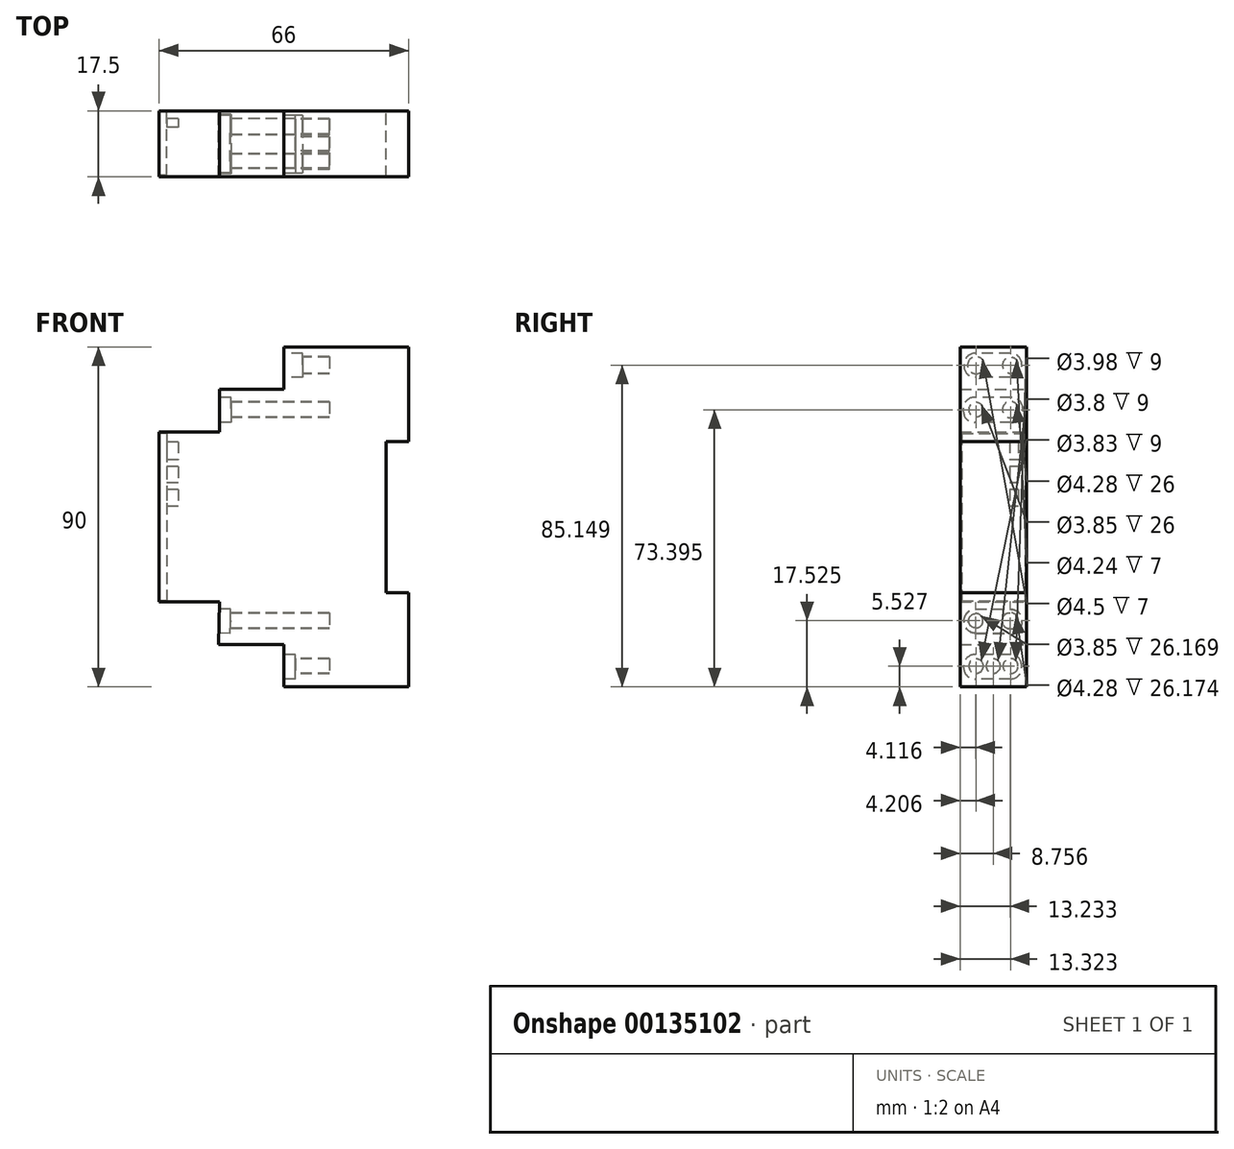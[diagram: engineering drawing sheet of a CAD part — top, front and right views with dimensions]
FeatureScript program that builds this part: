
annotation { "Feature Type Name" : "Feature", "Feature Type Description" : "" }
export const myFeature = defineFeature(function(context is Context, id is Id, definition is map)
    precondition{}
    {
        {
            var Q0;
            Q0=qCreatedBy(makeId("Front.planeOp"),FACE);
            var sketch = newSketch(context, id + "F0", { "sketchPlane" : qUnion([Q0])});
            skLineSegment(sketch, "E0.bottom", {"start": v(-62.04, 123.6) * mm, "end": v(-29.04, 123.6) * mm});
            skLineSegment(sketch, "E0.top", {"start": v(-62.04, 33.6) * mm, "end": v(-29.04, 33.6) * mm});
            skLineSegment(sketch, "E0.left", {"start": v(-95.04, 101.1) * mm, "end": v(-95.04, 56.1) * mm});
            skLineSegment(sketch, "E0.right", {"start": v(-29.04, 123.6) * mm, "end": v(-29.04, 98.6) * mm});
            skLineSegment(sketch, "E1", {"start": v(-62.04, 123.6) * mm, "end": v(-62.04, 112.34) * mm});
            skLineSegment(sketch, "E2", {"start": v(-62.04, 112.34) * mm, "end": v(-79.04, 112.34) * mm});
            skLineSegment(sketch, "E3", {"start": v(-79.04, 112.34) * mm, "end": v(-79.04, 101.1) * mm});
            skLineSegment(sketch, "E4", {"start": v(-79.04, 101.1) * mm, "end": v(-95.04, 101.1) * mm});
            skLineSegment(sketch, "E5", {"start": v(-95.04, 56.1) * mm, "end": v(-79.04, 56.1) * mm});
            skLineSegment(sketch, "E6", {"start": v(-79.04, 56.1) * mm, "end": v(-79.31, 44.84) * mm});
            skLineSegment(sketch, "E7", {"start": v(-79.31, 44.84) * mm, "end": v(-62.04, 44.84) * mm});
            skLineSegment(sketch, "E8", {"start": v(-62.04, 44.84) * mm, "end": v(-62.04, 33.6) * mm});
            skPoint(sketch, "E9.orphan", {"position": v(-95.04, 123.6) * mm});
            skPoint(sketch, "E10.orphan", {"position": v(-95.04, 33.6) * mm});
            skLineSegment(sketch, "E11", {"start": v(-29.04, 98.6) * mm, "end": v(-35.04, 98.6) * mm});
            skLineSegment(sketch, "E12", {"start": v(-35.04, 98.6) * mm, "end": v(-35.04, 58.6) * mm});
            skLineSegment(sketch, "E13", {"start": v(-35.04, 58.6) * mm, "end": v(-29.04, 58.6) * mm});
            skLineSegment(sketch, "E14.trimOffspring", {"start": v(-29.04, 58.6) * mm, "end": v(-29.04, 33.6) * mm});
            skSolve(sketch);
        }
        {
            var Q0;
            Q0=makeQuery(id+"F0.imprint","IMPRINT",FACE,{"disambiguationData":[TD([[makeQuery(id+"F0.imprint","IMPRINT",EDGE,{"derivedFrom":sQuery(id+"F0.wireOp",EDGE,"E0.bottom")}),-1.0]])]});
            extrude(context, id + "F1", {"entities" : qUnion([Q0]), "depth" : 17.5 * mm});
        }
        {
            var Q0;
            Q0=makeQuery(id+"F1.opExtrude","SWEPT_FACE",FACE,{"disambiguationData":[OSD([sQuery(id+"F0.wireOp",EDGE,"E0.left")])]});
            var sketch = newSketch(context, id + "F2", { "sketchPlane" : qUnion([Q0])});
            skCircle(sketch, "E15", {"center": v(4.18, 106.99) * mm, "radius": 2.14 * mm});
            skCircle(sketch, "E16", {"center": v(13.3, 106.99) * mm, "radius": 1.93 * mm});
            skCircle(sketch, "E17", {"center": v(13.3, 118.74) * mm, "radius": 2.25 * mm});
            skCircle(sketch, "E18", {"center": v(4.18, 118.74) * mm, "radius": 2.12 * mm});
            skCircle(sketch, "E19", {"center": v(4.18, 39.12) * mm, "radius": 1.99 * mm});
            skCircle(sketch, "E20", {"center": v(13.3, 39.12) * mm, "radius": 1.91 * mm});
            skCircle(sketch, "E21", {"center": v(8.74, 39.12) * mm, "radius": 1.9 * mm});
            skCircle(sketch, "E22", {"center": v(4.27, 51.11) * mm, "radius": 2.14 * mm});
            skCircle(sketch, "E23", {"center": v(13.38, 51.11) * mm, "radius": 1.93 * mm});
            skSolve(sketch);
        }
        {
            var Q0;
            Q0=makeQuery(id+"F1.opExtrude","SWEPT_FACE",FACE,{"disambiguationData":[OSD([sQuery(id+"F0.wireOp",EDGE,"E1")])]});
            var sketch = newSketch(context, id + "F3", { "sketchPlane" : qUnion([Q0])});
            skLineSegment(sketch, "E24.bottom", {"start": v(4.2, 121.92) * mm, "end": v(13.5, 121.92) * mm});
            skLineSegment(sketch, "E24.top", {"start": v(4.2, 115.51) * mm, "end": v(13.5, 115.51) * mm});
            skLineSegment(sketch, "E24.left", {"start": v(1.2, 118.92) * mm, "end": v(1.2, 118.51) * mm});
            skLineSegment(sketch, "E24.right", {"start": v(16.5, 118.92) * mm, "end": v(16.5, 118.51) * mm});
            skPoint(sketch, "E25.visualSharp", {"position": v(1.2, 121.92) * mm});
            skArc(sketch, "E25.filletArc", {"start": v(4.2, 121.92) * mm, "mid": v(2.09, 121.04) * mm, "end": v(1.2, 118.92) * mm});
            skPoint(sketch, "E26.visualSharp", {"position": v(1.2, 115.51) * mm});
            skArc(sketch, "E26.filletArc", {"start": v(1.2, 118.51) * mm, "mid": v(2.09, 116.39) * mm, "end": v(4.2, 115.51) * mm});
            skPoint(sketch, "E27.visualSharp", {"position": v(16.5, 115.51) * mm});
            skArc(sketch, "E27.filletArc", {"start": v(13.5, 115.51) * mm, "mid": v(15.61, 116.39) * mm, "end": v(16.5, 118.51) * mm});
            skPoint(sketch, "E28.visualSharp", {"position": v(16.5, 121.92) * mm});
            skArc(sketch, "E28.filletArc", {"start": v(16.5, 118.92) * mm, "mid": v(15.61, 121.04) * mm, "end": v(13.5, 121.92) * mm});
            skSolve(sketch);
        }
        {
            var Q0;
            Q0=makeQuery(id+"F3.imprint","IMPRINT",FACE,{"disambiguationData":[TD([[makeQuery(id+"F3.imprint","IMPRINT",EDGE,{"derivedFrom":sQuery(id+"F3.wireOp",EDGE,"E24.bottom")}),-1.0]])]});
            extrude(context, id + "F4", {"entities" : qUnion([Q0]), "operationType" : NewBodyOperationType.REMOVE, "oppositeDirection" : true, "depth" : 5 * mm});
        }
        {
            var Q0;
            Q0=makeQuery(id+"F1.opExtrude","SWEPT_FACE",FACE,{"disambiguationData":[OSD([sQuery(id+"F0.wireOp",EDGE,"E3")])]});
            var sketch = newSketch(context, id + "F5", { "sketchPlane" : qUnion([Q0])});
            skLineSegment(sketch, "E29.bottom", {"start": v(3.93, 110.28) * mm, "end": v(13.66, 110.28) * mm});
            skLineSegment(sketch, "E29.top", {"start": v(3.93, 103.59) * mm, "end": v(13.66, 103.59) * mm});
            skLineSegment(sketch, "E29.left", {"start": v(0.93, 107.28) * mm, "end": v(0.93, 106.59) * mm});
            skLineSegment(sketch, "E29.right", {"start": v(16.66, 107.28) * mm, "end": v(16.66, 106.59) * mm});
            skPoint(sketch, "E30.visualSharp", {"position": v(0.93, 110.28) * mm});
            skArc(sketch, "E30.filletArc", {"start": v(3.93, 110.28) * mm, "mid": v(1.81, 109.4) * mm, "end": v(0.93, 107.28) * mm});
            skPoint(sketch, "E31.visualSharp", {"position": v(0.93, 103.59) * mm});
            skArc(sketch, "E31.filletArc", {"start": v(0.93, 106.59) * mm, "mid": v(1.81, 104.47) * mm, "end": v(3.93, 103.59) * mm});
            skPoint(sketch, "E32.visualSharp", {"position": v(16.66, 103.59) * mm});
            skArc(sketch, "E32.filletArc", {"start": v(13.66, 103.59) * mm, "mid": v(15.78, 104.47) * mm, "end": v(16.66, 106.59) * mm});
            skPoint(sketch, "E33.visualSharp", {"position": v(16.66, 110.28) * mm});
            skArc(sketch, "E33.filletArc", {"start": v(16.66, 107.28) * mm, "mid": v(15.78, 109.4) * mm, "end": v(13.66, 110.28) * mm});
            skSolve(sketch);
        }
        {
            var Q0;
            Q0=makeQuery(id+"F5.imprint","IMPRINT",FACE,{"disambiguationData":[TD([[makeQuery(id+"F5.imprint","IMPRINT",EDGE,{"derivedFrom":sQuery(id+"F5.wireOp",EDGE,"E29.bottom")}),-1.0]])]});
            extrude(context, id + "F6", {"entities" : qUnion([Q0]), "operationType" : NewBodyOperationType.REMOVE, "oppositeDirection" : true, "depth" : 3 * mm});
        }
        {
            var Q0;
            Q0=makeQuery(id+"F1.opExtrude","SWEPT_FACE",FACE,{"disambiguationData":[OSD([sQuery(id+"F0.wireOp",EDGE,"E8")])]});
            var sketch = newSketch(context, id + "F7", { "sketchPlane" : qUnion([Q0])});
            skLineSegment(sketch, "E34.bottom", {"start": v(4.23, 35.68) * mm, "end": v(13.57, 35.68) * mm});
            skLineSegment(sketch, "E34.top", {"start": v(4.23, 42.21) * mm, "end": v(13.57, 42.21) * mm});
            skLineSegment(sketch, "E34.left", {"start": v(1.23, 38.68) * mm, "end": v(1.23, 39.21) * mm});
            skLineSegment(sketch, "E34.right", {"start": v(16.57, 38.68) * mm, "end": v(16.57, 39.21) * mm});
            skPoint(sketch, "E35.visualSharp", {"position": v(16.57, 42.21) * mm});
            skArc(sketch, "E35.filletArc", {"start": v(16.57, 39.21) * mm, "mid": v(15.7, 41.34) * mm, "end": v(13.57, 42.21) * mm});
            skPoint(sketch, "E36.visualSharp", {"position": v(16.57, 35.68) * mm});
            skArc(sketch, "E36.filletArc", {"start": v(13.57, 35.68) * mm, "mid": v(15.7, 36.56) * mm, "end": v(16.57, 38.68) * mm});
            skPoint(sketch, "E37.visualSharp", {"position": v(1.23, 35.68) * mm});
            skArc(sketch, "E37.filletArc", {"start": v(1.23, 38.68) * mm, "mid": v(2.1, 36.56) * mm, "end": v(4.23, 35.68) * mm});
            skPoint(sketch, "E38.visualSharp", {"position": v(1.23, 42.21) * mm});
            skArc(sketch, "E38.filletArc", {"start": v(4.23, 42.21) * mm, "mid": v(2.1, 41.34) * mm, "end": v(1.23, 39.21) * mm});
            skSolve(sketch);
        }
        {
            var Q0;
            Q0=makeQuery(id+"F7.imprint","IMPRINT",FACE,{"disambiguationData":[TD([[makeQuery(id+"F7.imprint","IMPRINT",EDGE,{"derivedFrom":sQuery(id+"F7.wireOp",EDGE,"E34.bottom")}),1.0]])]});
            extrude(context, id + "F8", {"entities" : qUnion([Q0]), "operationType" : NewBodyOperationType.REMOVE, "oppositeDirection" : true, "depth" : 3 * mm});
        }
        {
            var Q0;
            Q0=makeQuery(id+"F1.opExtrude","SWEPT_FACE",FACE,{"disambiguationData":[OSD([sQuery(id+"F0.wireOp",EDGE,"E0.left")])]});
            var sketch = newSketch(context, id + "F9", { "sketchPlane" : qUnion([Q0])});
            skLineSegment(sketch, "E39.bottom", {"start": v(17.09, 100.66) * mm, "end": v(0.28, 100.66) * mm});
            skLineSegment(sketch, "E39.top", {"start": v(17.09, 56.37) * mm, "end": v(0.28, 56.37) * mm});
            skLineSegment(sketch, "E39.left", {"start": v(17.09, 100.66) * mm, "end": v(17.09, 56.37) * mm});
            skLineSegment(sketch, "E39.right", {"start": v(0.28, 100.66) * mm, "end": v(0.28, 56.37) * mm});
            skSolve(sketch);
        }
        {
            var Q0;
            Q0=makeQuery(id+"F9.imprint","IMPRINT",FACE,{"disambiguationData":[TD([[makeQuery(id+"F9.imprint","IMPRINT",EDGE,{"derivedFrom":sQuery(id+"F9.wireOp",EDGE,"E39.bottom")}),1.0]])]});
            extrude(context, id + "F10", {"entities" : qUnion([Q0]), "operationType" : NewBodyOperationType.REMOVE, "oppositeDirection" : true, "depth" : 2 * mm});
        }
        {
            var Q0;
            Q0=makeQuery(id+"F2.imprint","IMPRINT",FACE,{"disambiguationData":[TD([[makeQuery(id+"F2.imprint","IMPRINT",EDGE,{"derivedFrom":sQuery(id+"F2.wireOp",EDGE,"E18")}),1.0]])]});
            var Q1;
            Q1=makeQuery(id+"F2.imprint","IMPRINT",FACE,{"disambiguationData":[TD([[makeQuery(id+"F2.imprint","IMPRINT",EDGE,{"derivedFrom":sQuery(id+"F2.wireOp",EDGE,"E17")}),1.0]])]});
            var Q2;
            Q2=makeQuery(id+"F2.imprint","IMPRINT",FACE,{"disambiguationData":[TD([[makeQuery(id+"F2.imprint","IMPRINT",EDGE,{"derivedFrom":sQuery(id+"F2.wireOp",EDGE,"E15")}),1.0]])]});
            var Q3;
            Q3=makeQuery(id+"F2.imprint","IMPRINT",FACE,{"disambiguationData":[TD([[makeQuery(id+"F2.imprint","IMPRINT",EDGE,{"derivedFrom":sQuery(id+"F2.wireOp",EDGE,"E16")}),1.0]])]});
            var Q4;
            Q4=makeQuery(id+"F2.imprint","IMPRINT",FACE,{"disambiguationData":[TD([[makeQuery(id+"F2.imprint","IMPRINT",EDGE,{"derivedFrom":sQuery(id+"F2.wireOp",EDGE,"E22")}),1.0]])]});
            var Q5;
            Q5=makeQuery(id+"F2.imprint","IMPRINT",FACE,{"disambiguationData":[TD([[makeQuery(id+"F2.imprint","IMPRINT",EDGE,{"derivedFrom":sQuery(id+"F2.wireOp",EDGE,"E23")}),1.0]])]});
            var Q6;
            Q6=makeQuery(id+"F2.imprint","IMPRINT",FACE,{"disambiguationData":[TD([[makeQuery(id+"F2.imprint","IMPRINT",EDGE,{"derivedFrom":sQuery(id+"F2.wireOp",EDGE,"E19")}),1.0]])]});
            var Q7;
            Q7=makeQuery(id+"F2.imprint","IMPRINT",FACE,{"disambiguationData":[TD([[makeQuery(id+"F2.imprint","IMPRINT",EDGE,{"derivedFrom":sQuery(id+"F2.wireOp",EDGE,"E21")}),1.0]])]});
            var Q8;
            Q8=makeQuery(id+"F2.imprint","IMPRINT",FACE,{"disambiguationData":[TD([[makeQuery(id+"F2.imprint","IMPRINT",EDGE,{"derivedFrom":sQuery(id+"F2.wireOp",EDGE,"E20")}),1.0]])]});
            extrude(context, id + "F11", {"entities" : qUnion([Q0, Q1, Q2, Q3, Q4, Q5, Q6, Q7, Q8]), "operationType" : NewBodyOperationType.REMOVE, "oppositeDirection" : true, "depth" : 45 * mm});
        }
        {
            var Q0;
            Q0=makeQuery(id+"F1.opExtrude","SWEPT_FACE",FACE,{"disambiguationData":[OSD([sQuery(id+"F0.wireOp",EDGE,"E6")])]});
            var sketch = newSketch(context, id + "F12", { "sketchPlane" : qUnion([Q0])});
            skLineSegment(sketch, "E40.bottom", {"start": v(13.44, 52.27) * mm, "end": v(4.22, 52.27) * mm});
            skLineSegment(sketch, "E40.top", {"start": v(13.44, 45.9) * mm, "end": v(4.22, 45.9) * mm});
            skLineSegment(sketch, "E40.left", {"start": v(16.44, 49.27) * mm, "end": v(16.44, 48.9) * mm});
            skLineSegment(sketch, "E40.right", {"start": v(1.22, 49.27) * mm, "end": v(1.22, 48.9) * mm});
            skPoint(sketch, "E41.visualSharp", {"position": v(16.44, 52.27) * mm});
            skArc(sketch, "E41.filletArc", {"start": v(16.44, 49.27) * mm, "mid": v(15.56, 51.4) * mm, "end": v(13.44, 52.27) * mm});
            skPoint(sketch, "E42.visualSharp", {"position": v(16.44, 45.9) * mm});
            skArc(sketch, "E42.filletArc", {"start": v(13.44, 45.9) * mm, "mid": v(15.56, 46.77) * mm, "end": v(16.44, 48.9) * mm});
            skPoint(sketch, "E43.visualSharp", {"position": v(1.22, 45.9) * mm});
            skArc(sketch, "E43.filletArc", {"start": v(1.22, 48.9) * mm, "mid": v(2.1, 46.77) * mm, "end": v(4.22, 45.9) * mm});
            skPoint(sketch, "E44.visualSharp", {"position": v(1.22, 52.27) * mm});
            skArc(sketch, "E44.filletArc", {"start": v(4.22, 52.27) * mm, "mid": v(2.1, 51.4) * mm, "end": v(1.22, 49.27) * mm});
            skSolve(sketch);
        }
        {
            var Q0;
            Q0 = qSketchRegion(id + "F12", true);
            extrude(context, id + "F13", {"entities" : qUnion([Q0]), "operationType" : NewBodyOperationType.REMOVE, "oppositeDirection" : true, "depth" : 3 * mm});
        }
        {
            var Q0;
            Q0=makeQuery(id+"F10.boolean.opBoolean","COPY",FACE,{"derivedFrom":makeQuery(id+"F10.opExtrude","CAP_FACE",FACE,{"disambiguationData":[OSD([sQuery(id+"F9.wireOp",EDGE,"E39.bottom"),sQuery(id+"F9.wireOp",EDGE,"E39.top"),sQuery(id+"F9.wireOp",EDGE,"E39.left"),sQuery(id+"F9.wireOp",EDGE,"E39.right")])],"isStart":false})});
            var sketch = newSketch(context, id + "F14", { "sketchPlane" : qUnion([Q0])});
            skLineSegment(sketch, "E45.bottom", {"start": v(2.1, 98.43) * mm, "end": v(4.37, 98.43) * mm});
            skLineSegment(sketch, "E45.top", {"start": v(2.1, 93.73) * mm, "end": v(4.37, 93.73) * mm});
            skLineSegment(sketch, "E45.left", {"start": v(2.1, 98.43) * mm, "end": v(2.1, 93.73) * mm});
            skLineSegment(sketch, "E45.right", {"start": v(4.37, 98.43) * mm, "end": v(4.37, 93.73) * mm});
            skLineSegment(sketch, "E46.bottom", {"start": v(2.1, 91.88) * mm, "end": v(4.37, 91.88) * mm});
            skLineSegment(sketch, "E46.top", {"start": v(2.1, 87.56) * mm, "end": v(4.37, 87.56) * mm});
            skLineSegment(sketch, "E46.left", {"start": v(2.1, 91.88) * mm, "end": v(2.1, 87.56) * mm});
            skLineSegment(sketch, "E46.right", {"start": v(4.37, 91.88) * mm, "end": v(4.37, 87.56) * mm});
            skLineSegment(sketch, "E47.bottom", {"start": v(2.1, 85.9) * mm, "end": v(4.37, 85.9) * mm});
            skLineSegment(sketch, "E47.top", {"start": v(2.1, 81.37) * mm, "end": v(4.37, 81.37) * mm});
            skLineSegment(sketch, "E47.left", {"start": v(2.1, 85.9) * mm, "end": v(2.1, 81.37) * mm});
            skLineSegment(sketch, "E47.right", {"start": v(4.37, 85.9) * mm, "end": v(4.37, 81.37) * mm});
            skSolve(sketch);
        }
        {
            var Q0;
            Q0=makeQuery(id+"F14.imprint","IMPRINT",FACE,{"disambiguationData":[TD([[makeQuery(id+"F14.imprint","IMPRINT",EDGE,{"derivedFrom":sQuery(id+"F14.wireOp",EDGE,"E45.bottom")}),-1.0]])]});
            var Q1;
            Q1=makeQuery(id+"F14.imprint","IMPRINT",FACE,{"disambiguationData":[TD([[makeQuery(id+"F14.imprint","IMPRINT",EDGE,{"derivedFrom":sQuery(id+"F14.wireOp",EDGE,"E46.bottom")}),-1.0]])]});
            var Q2;
            Q2=makeQuery(id+"F14.imprint","IMPRINT",FACE,{"disambiguationData":[TD([[makeQuery(id+"F14.imprint","IMPRINT",EDGE,{"derivedFrom":sQuery(id+"F14.wireOp",EDGE,"E47.bottom")}),-1.0]])]});
            extrude(context, id + "F15", {"entities" : qUnion([Q0, Q1, Q2]), "operationType" : NewBodyOperationType.REMOVE, "oppositeDirection" : true, "depth" : 3 * mm});
        }
    });
